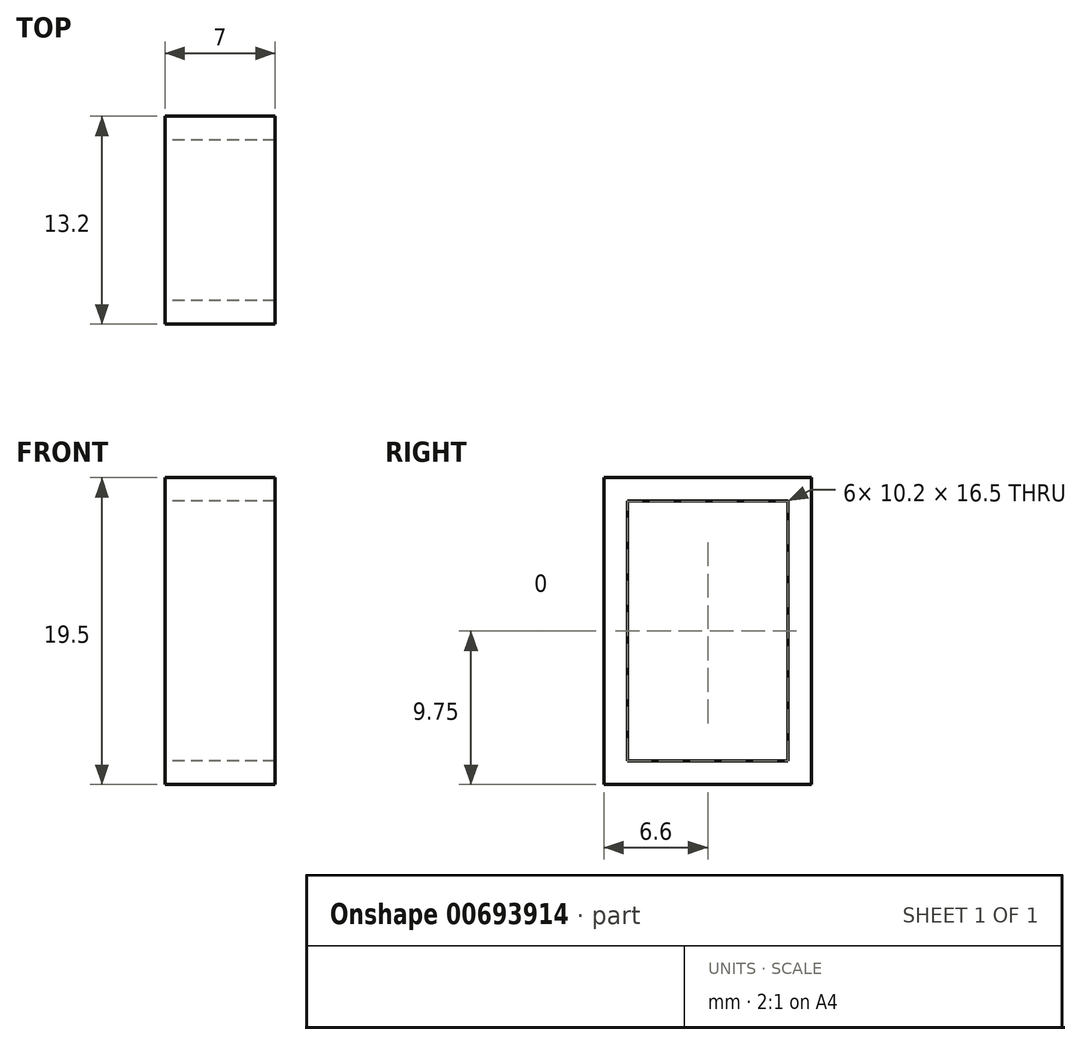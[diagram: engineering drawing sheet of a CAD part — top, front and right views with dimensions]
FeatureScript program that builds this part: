
annotation { "Feature Type Name" : "Feature", "Feature Type Description" : "" }
export const myFeature = defineFeature(function(context is Context, id is Id, definition is map)
    precondition{}
    {
        {
            var Q0;
            Q0=qCreatedBy(makeId("Right.planeOp"),FACE);
            var sketch = newSketch(context, id + "F0", { "sketchPlane" : qUnion([Q0])});
            skLineSegment(sketch, "E0.bottom", {"start": v(5.1, 8.25) * mm, "end": v(-5.1, 8.25) * mm});
            skLineSegment(sketch, "E0.top", {"start": v(5.1, -8.25) * mm, "end": v(-5.1, -8.25) * mm});
            skLineSegment(sketch, "E0.left", {"start": v(5.1, 8.25) * mm, "end": v(5.1, -8.25) * mm});
            skLineSegment(sketch, "E0.right", {"start": v(-5.1, 8.25) * mm, "end": v(-5.1, -8.25) * mm});
            skPoint(sketch, "E0.middle", {"position": v(0, 0) * mm});
            skLineSegment(sketch, "E1.bottom", {"start": v(6.6, 9.75) * mm, "end": v(-6.6, 9.75) * mm});
            skLineSegment(sketch, "E1.top", {"start": v(6.6, -9.75) * mm, "end": v(-6.6, -9.75) * mm});
            skLineSegment(sketch, "E1.left", {"start": v(6.6, 9.75) * mm, "end": v(6.6, -9.75) * mm});
            skLineSegment(sketch, "E1.right", {"start": v(-6.6, 9.75) * mm, "end": v(-6.6, -9.75) * mm});
            skSolve(sketch);
        }
        {
            var Q0;
            Q0=makeQuery(id+"F0.imprint","IMPRINT",FACE,{"disambiguationData":[TD([[makeQuery(id+"F0.imprint","IMPRINT",EDGE,{"derivedFrom":sQuery(id+"F0.wireOp",EDGE,"E0.bottom")}),-1.0]])]});
            extrude(context, id + "F1", {"entities" : qUnion([Q0]), "depth" : 7 * mm, "offsetDistance" : 25 * mm});
        }
    });
